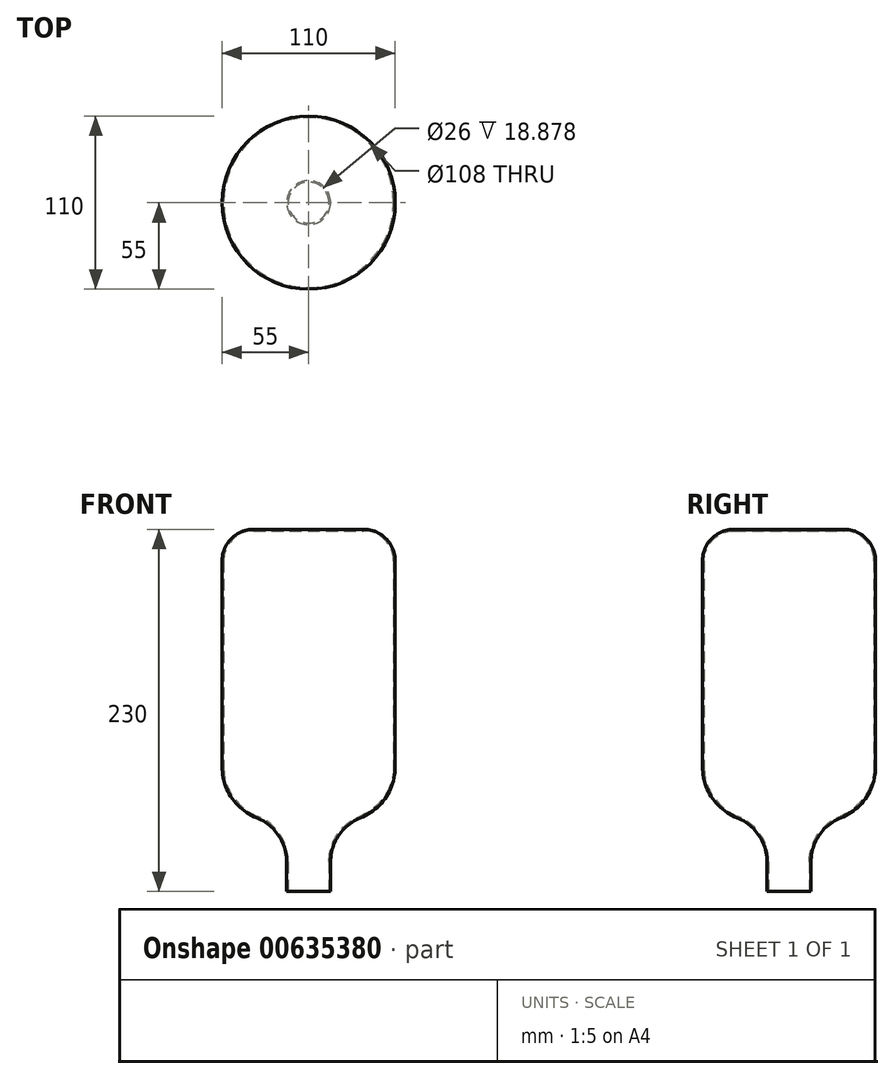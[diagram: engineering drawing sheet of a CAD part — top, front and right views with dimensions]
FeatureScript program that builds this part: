
annotation { "Feature Type Name" : "Feature", "Feature Type Description" : "" }
export const myFeature = defineFeature(function(context is Context, id is Id, definition is map)
    precondition{}
    {
        {
            var Q0;
            Q0=qCreatedBy(makeId("Front.planeOp"),FACE);
            var sketch = newSketch(context, id + "F0", { "sketchPlane" : qUnion([Q0])});
            skLineSegment(sketch, "E0", {"start": v(0, 0) * mm, "end": v(14, 0) * mm});
            skLineSegment(sketch, "E1", {"start": v(14, 0) * mm, "end": v(14, 18.88) * mm});
            skArc(sketch, "E2", {"start": v(14, 18.88) * mm, "mid": v(19.18, 35.73) * mm, "end": v(32.92, 46.76) * mm});
            skArc(sketch, "E3", {"start": v(32.92, 46.76) * mm, "mid": v(48.96, 59.63) * mm, "end": v(55, 79.29) * mm});
            skLineSegment(sketch, "E4", {"start": v(55, 79.29) * mm, "end": v(55, 210) * mm});
            skArc(sketch, "E5", {"start": v(55, 210) * mm, "mid": v(49.14, 224.14) * mm, "end": v(35, 230) * mm});
            skLineSegment(sketch, "E6", {"start": v(35, 230) * mm, "end": v(0, 230) * mm});
            skLineSegment(sketch, "E7", {"start": v(0, 0) * mm, "end": v(0, 230) * mm});
            skSolve(sketch);
        }
        {
            var Q0;
            Q0 = qSketchRegion(id + "F0", true);
            var Q1;
            Q1=sQuery(id+"F0.wireOp",EDGE,"E7");
            revolve(context, id + "F1", {"surfaceOperationType" : NewSurfaceOperationType.NEW, "entities" : qUnion([Q0]), "axis" : qUnion([Q1]), "revolveType" : RevolveType.FULL});
        }
        {
            var Q0;
            Q0=makeQuery(id+"F1.opRevolve","SWEPT_FACE",FACE,{"disambiguationData":[OSD([sQuery(id+"F0.wireOp",EDGE,"E0")])]});
            shell(context, id + "F2", {"entities" : qUnion([Q0]), "thickness" : 1 * mm});
        }
    });
